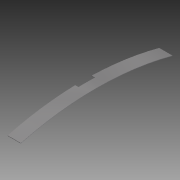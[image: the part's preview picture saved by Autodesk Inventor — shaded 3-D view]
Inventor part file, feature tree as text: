
AUTODESK INVENTOR PART (.ipt)
format: ipt  version: 2013 (Build 170138000, 138)  size: 122,368 bytes
history: native  units: in
note: dims shown in document units (in); Inventor stores cm internally (conversion verified against a paired STEP export)
features: extrude x2, plane x2, sketch x2, projected_geometry x1, other x1
ambient origin geometry x8: Origin, YZ Plane, XZ Plane, XY Plane, X Axis, Y Axis, Z Axis, Center Point
feature tree (8):
  extrude  "Extrusion5"  Depth=46.0in
  plane  "Work Plane2"
  extrude  "Extrusion6"  Depth=4.0in TaperAngle=0.0deg
  plane  "Work Plane3"
  sketch  "Sketch7"  dims[d2=0.125in d36=46.0in]
  sketch  "Sketch8"  dims[d37=0.125in d38=4.0in d39=0.0in d40=1.0in d41=5.0in d42=20.5in d43=20.5in d44=4.0in d45=0.0in d46=3.0in d47=23.0in d48=23.0in]
  projected_geometry  "Projected Loop3"
  other  "Definition1"
